# Revit family: Sanitary_Showers_hansgrohe_04928USA-Club-Overhead-shower-100-3jet-1_7676767
name_source: partatom
category: Plumbing Fixtures
revit_build: Autodesk Revit 2018 (Build: 20170223_1515(x64)
units: mm (PartAtom-declared; Revit-internal decimal feet)

## family parameters
Always vertical = No
Cut with Voids When Loaded = No
OmniClass Number = 23.45.05.14.17
OmniClass Title = Showers
Part Type = Normal
Room Calculation Point = No
Round Connector Dimension = Use Diameter
Shared = No
Work Plane-Based = Yes

## types (2) — shared parameters
BIMobject category = Showers
Default Elevation = 1219.2 mm  [stored 4 ft]
Description = Club Overhead shower 100 3jet 1.5 GPM
Design country = Germany
EAN code = 4059625341865
Edition number = 1
GTIN code = https://4059625342084
IFC Classification = Sanitary Terminal
Installation instructions = https://www.hansgrohe.com
Manufacturer = Hansgrohe
Manufacturer country = Germany
Manufacturer name = hansgrohe
Material main = Chrome
Model = 04928USA
OmniClass Code = 23-31 17 00
OmniClass Description = Showers
Product Guid = 50675f79-208a-44e9-aea6-537d46bc172b
Product SKU = 04928USA
Product data url = https://bimobject.com
Product family = Club
Product group = Overhead showers
Product name = 04928USA Club Overhead shower 100 3jet 1.5 GPM
Product url = https://www.hansgrohe.com
QR code = https://bimobject.com
URL = https://www.hansgrohe.com
Water  Inlet = 13 mm
Water Inlet Description = Water  Inlet 12.7mm

## per-type parameters (varying)
| type | Material |
| 000 Chrome | Hansgrohe - Metal - 000 Chrome |
| 820 Brushed Nickel | Hansgrohe - Metal - 820 Brushed Nickel |

note: [stored X ft] marks values corroborated as IEEE doubles in the binary element streams (Revit-internal decimal feet)

## geometry (parser evidence)
native form markers: Sweep x2
no freeform markers — native parametric forms only
